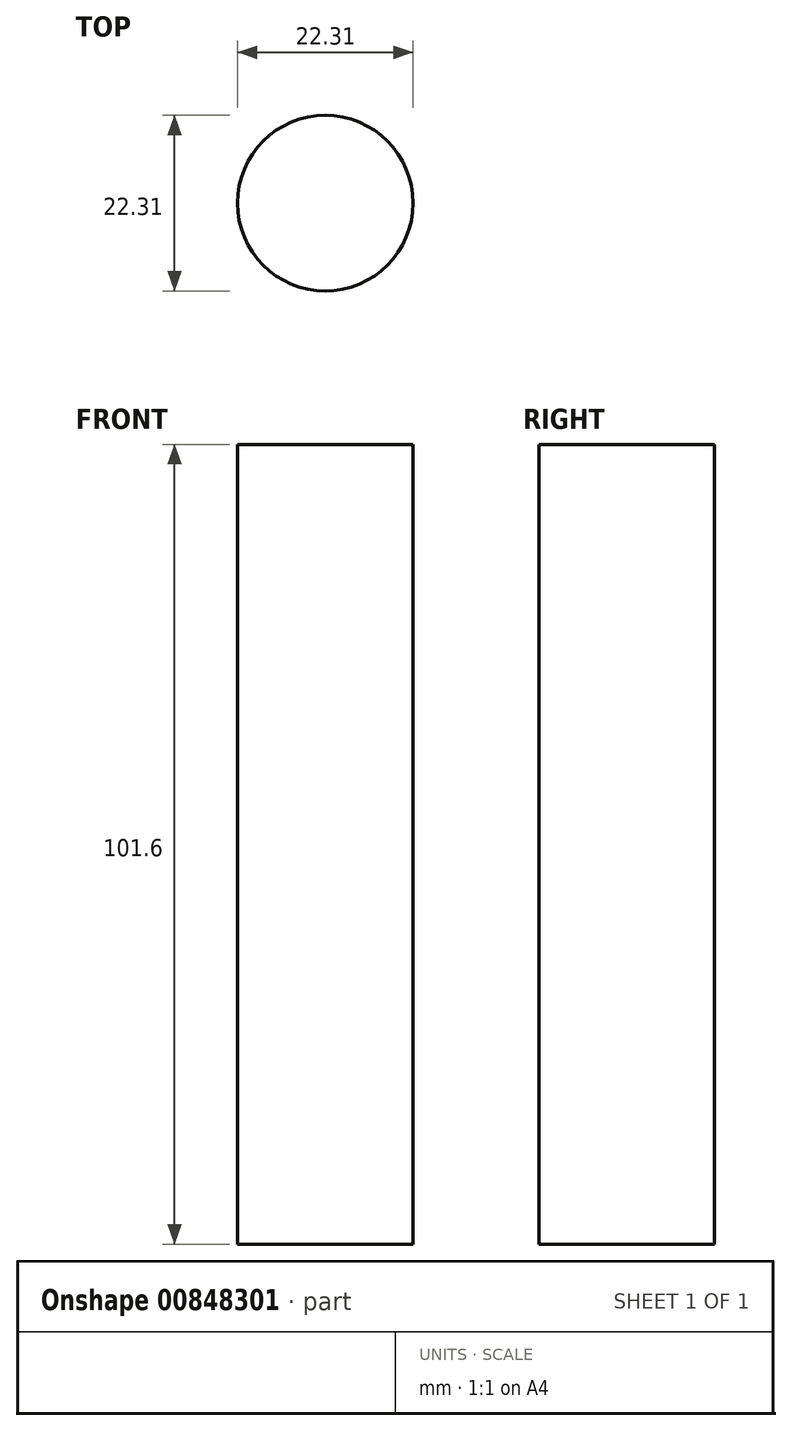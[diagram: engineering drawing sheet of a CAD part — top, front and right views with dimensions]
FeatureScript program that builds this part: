
annotation { "Feature Type Name" : "Feature", "Feature Type Description" : "" }
export const myFeature = defineFeature(function(context is Context, id is Id, definition is map)
    precondition{}
    {
        {
            var Q0;
            Q0=qCreatedBy(makeId("Top.planeOp"),FACE);
            var sketch = newSketch(context, id + "F0", { "sketchPlane" : qUnion([Q0])});
            skCircle(sketch, "E0", {"center": v(-46.32, -29.39) * mm, "radius": 11.15 * mm});
            skSolve(sketch);
        }
        {
            var Q0;
            Q0=makeQuery(id+"F0.imprint","IMPRINT",FACE,{"disambiguationData":[TD([[makeQuery(id+"F0.imprint","IMPRINT",EDGE,{"derivedFrom":sQuery(id+"F0.wireOp",EDGE,"E0")}),1.0]])]});
            extrude(context, id + "F1", {"entities" : qUnion([Q0]), "depth" : 101.6 * mm, "offsetDistance" : 25.4 * mm});
        }
    });
